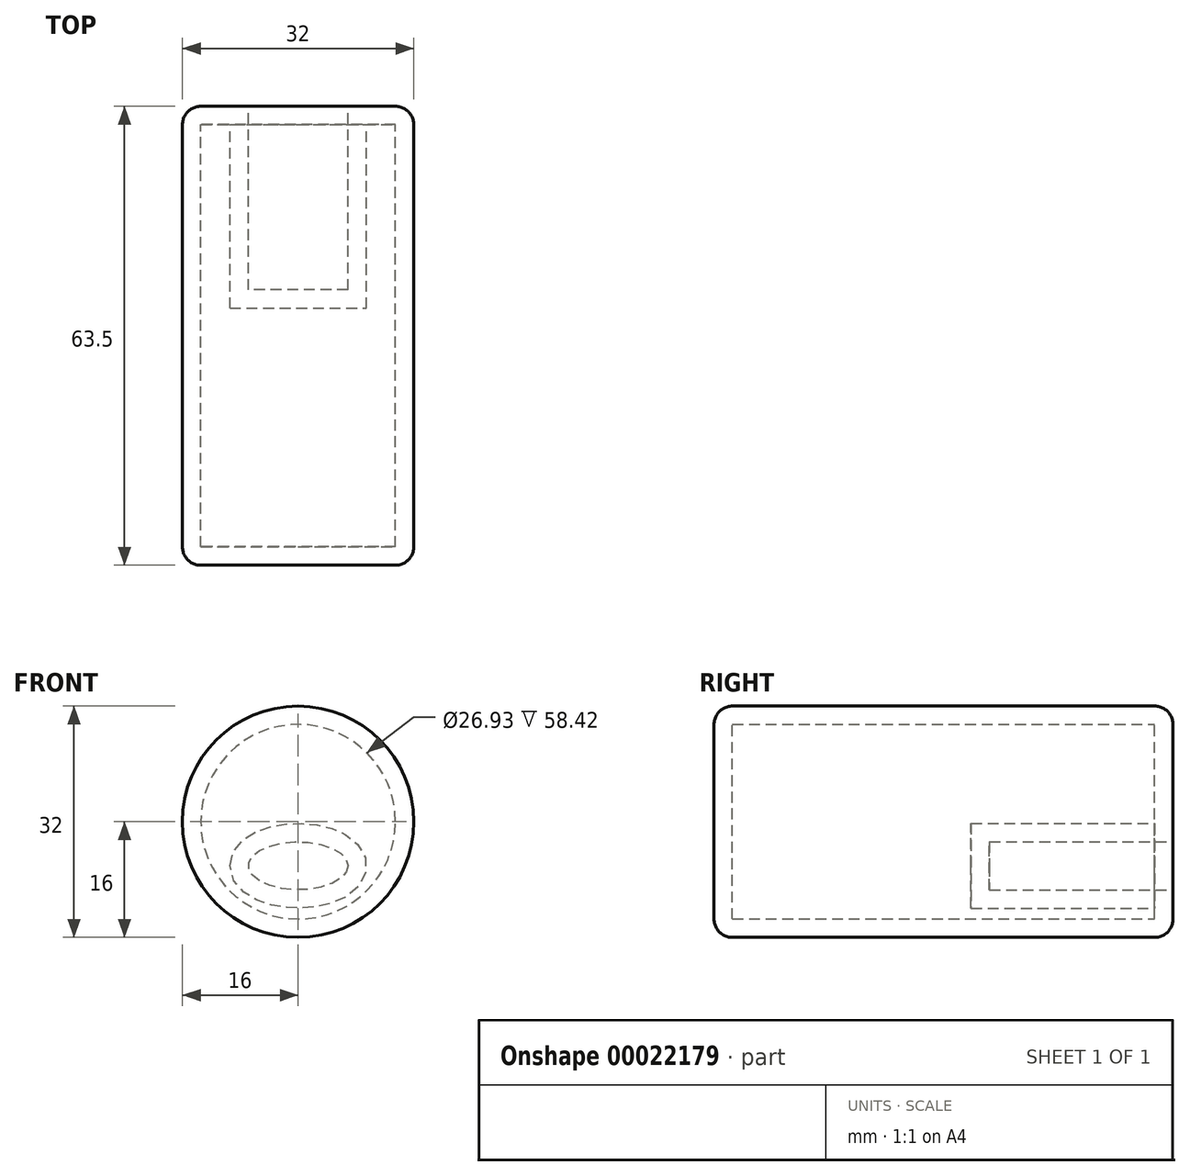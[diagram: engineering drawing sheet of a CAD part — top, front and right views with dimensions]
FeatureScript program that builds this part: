
annotation { "Feature Type Name" : "Feature", "Feature Type Description" : "" }
export const myFeature = defineFeature(function(context is Context, id is Id, definition is map)
    precondition{}
    {
        {
            var Q0;
            Q0=qCreatedBy(makeId("Front.planeOp"),FACE);
            var sketch = newSketch(context, id + "F0", { "sketchPlane" : qUnion([Q0])});
            skCircle(sketch, "E0", {"center": v(0, 0) * mm, "radius": 16 * mm});
            skSolve(sketch);
        }
        {
            var Q0;
            Q0=makeQuery(id+"F0.imprint","IMPRINT",FACE,{"disambiguationData":[TD([[makeQuery(id+"F0.imprint","IMPRINT",EDGE,{"derivedFrom":sQuery(id+"F0.wireOp",EDGE,"E0")}),1.0]])]});
            extrude(context, id + "F1", {"entities" : qUnion([Q0]), "depth" : 63.5 * mm});
        }
        {
            var Q0;
            Q0=makeQuery(id+"F1.opExtrude","CAP_EDGE",EDGE,{"disambiguationData":[OSD([sQuery(id+"F0.wireOp",EDGE,"E0")])],"isStart":false});
            var Q1;
            Q1=makeQuery(id+"F1.opExtrude","SWEPT_FACE",FACE,{"disambiguationData":[OSD([sQuery(id+"F0.wireOp",EDGE,"E0")])]});
            fillet(context, id + "F2", {"entities" : qUnion([Q0, Q1]), "radius" : 2.54 * mm, "tangentPropagation" : true, "allowEdgeOverflow" : false});
        }
        {
            var Q0;
            Q0=makeQuery(id+"F1.opExtrude","CAP_FACE",FACE,{"disambiguationData":[OSD([sQuery(id+"F0.wireOp",EDGE,"E0")])],"isStart":true});
            var sketch = newSketch(context, id + "F3", { "sketchPlane" : qUnion([Q0])});
            skEllipse(sketch, "E1", {"center": v(0, -6.09) * mm, "majorRadius": 6.9 * mm, "minorRadius": 3.32 * mm, "majorAxis": v(-1, 0)});
            skSolve(sketch);
        }
        {
            var Q0;
            Q0=makeQuery(id+"F3.imprint","IMPRINT",FACE,{"disambiguationData":[TD([[makeQuery(id+"F3.imprint","IMPRINT",EDGE,{"derivedFrom":sQuery(id+"F3.wireOp",EDGE,"E1")}),1.0]])]});
            extrude(context, id + "F4", {"entities" : qUnion([Q0]), "operationType" : NewBodyOperationType.REMOVE, "oppositeDirection" : true, "depth" : 25.4 * mm});
        }
        {
            var Q0;
            Q0=makeQuery(id+"F4.boolean.opBoolean","COPY",FACE,{"derivedFrom":makeQuery(id+"F4.opExtrude","CAP_FACE",FACE,{"disambiguationData":[OSD([sQuery(id+"F3.wireOp",EDGE,"E1")])],"isStart":false})});
            var Q1;
            Q1=makeQuery(id+"F1.opExtrude","SWEPT_BODY",BODY,{"disambiguationData":[OSD([sQuery(id+"F0.wireOp",EDGE,"E0")])]});
            shell(context, id + "F5", {"isHollow" : true, "entities" : qUnion([Q0]), "parts" : qUnion([Q1]), "thickness" : 2.54 * mm});
        }
    });
